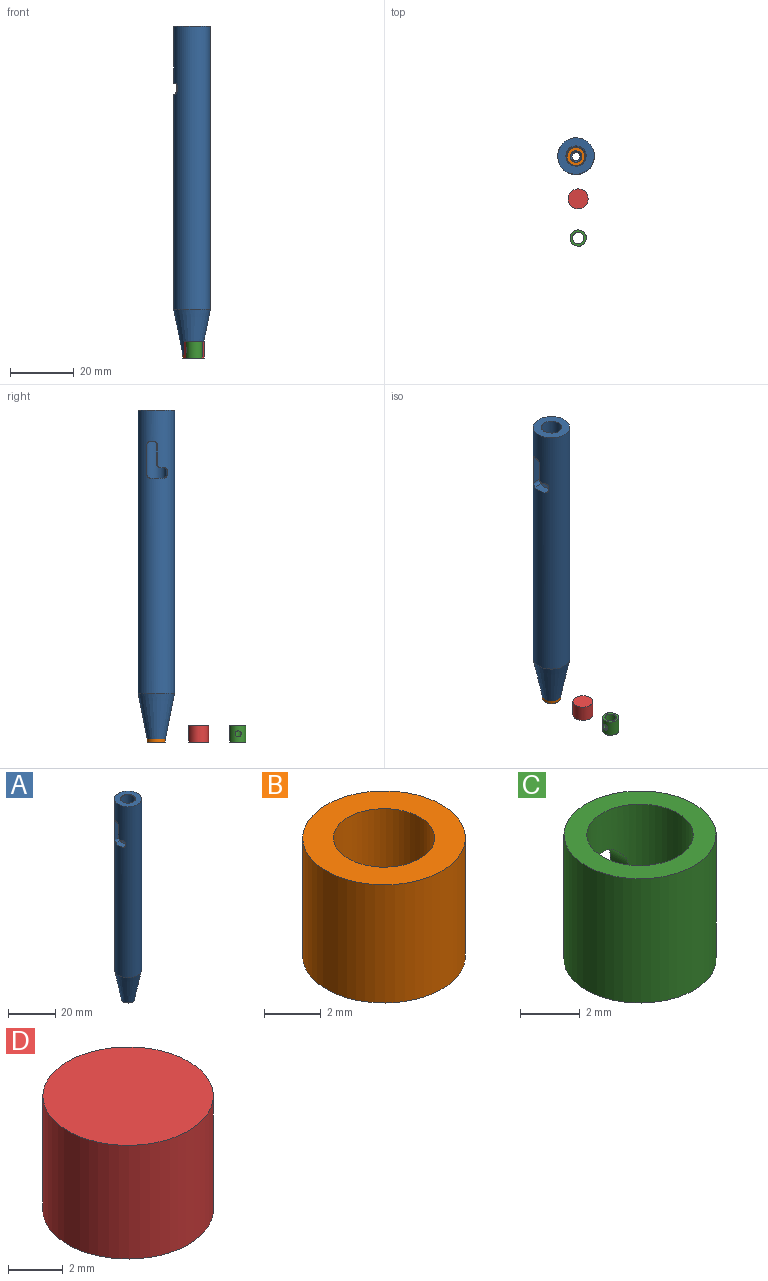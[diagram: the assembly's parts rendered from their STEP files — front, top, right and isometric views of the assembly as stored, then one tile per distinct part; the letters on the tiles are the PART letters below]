
ASSEMBLY  parts=4 mates=3
PART A: 22 faces, bbox 11.4x11.4x103.9 mm
  f0: cylinder r=1.78mm len=3.56mm, axis (0,0,-1), area 14.2mm2, adj f17,f20
  f1: cylinder r=3.17mm len=98.39mm, axis (0,0,-1), area 1893.3mm2, adj f3,f4,f5,f6,f7,f8,f10,f11
  f2: cylinder r=5.71mm len=88.61mm, axis (0,0,-1), area 3133.2mm2, adj f3,f4,f5,f6,f7,f8,f10,f11
  f3: plane 9.4x4.75mm, normal (0,-1,0), area 44.7mm2, adj f1,f2,f10,f15
  f4: plane 3.3x1.14mm, normal (0,0,-1), area 3.2mm2, adj f1,f2,f10,f11
  f5: plane 6.14x2.54mm, normal (0,1,0), area 15.6mm2, adj f1,f2,f11,f12
  f6: plane 3.21x0.99mm, normal (0,-0.08,-1), area 2.7mm2, adj f1,f2,f12,f13
  f7: plane 4.75x1.31mm, normal (0,1,0), area 6.2mm2, adj f1,f2,f13,f14
  f8: plane 4.32x3.39mm, normal (0,0,1), area 11.5mm2, adj f1,f2,f14,f15
  f9: plane 5.33x5.33mm, normal (0,0,-1), area 17.3mm2, adj f18,f19
  f10: cylinder r=1.02mm len=5.29mm, axis (-1,0,0), area 5.9mm2, adj f1,f2,f3,f4
  f11: cylinder r=1.02mm len=2.71mm, axis (-1,0,0), area 4.1mm2, adj f1,f2,f4,f5
  f12: cylinder r=1.02mm len=2.74mm, axis (-1,0,0), area 4.2mm2, adj f1,f2,f5,f6
  f13: cylinder r=1.02mm len=5.32mm, axis (-1,0,0), area 6.1mm2, adj f1,f2,f6,f7
  f14: cylinder r=1.02mm len=5.29mm, axis (1,0,0), area 5.9mm2, adj f1,f2,f7,f8
  f15: cylinder r=1.02mm len=5.29mm, axis (-1,0,0), area 5.9mm2, adj f1,f2,f3,f8
  f16: plane 11.43x11.43mm, normal (0,0,1), area 70.9mm2, adj f1,f2
  f17: plane 5.59x5.59mm, normal (0,0,1), area 14.6mm2, adj f0,f21
  f18: cone r=5.71mm half-angle=11.3deg, axis (0,0,1), area 409.3mm2, adj f2,f9
  f19: cylinder r=1.27mm len=3.3mm, axis (0,0,-1), area 26.3mm2, adj f9,f20
  f20: cone r=1.27mm half-angle=45deg, axis (0,0,1), area 6.9mm2, adj f0,f19
  f21: cone r=2.79mm half-angle=45deg, axis (0,0,1), area 10.1mm2, adj f1,f17
PART B: 4 faces, bbox 5.7x5.7x5.1 mm
  f0: cylinder r=1.78mm len=5.08mm, axis (0,0,-1), area 56.8mm2, adj f2,f3
  f1: cylinder r=2.86mm len=5.72mm, axis (0,0,-1), area 91.2mm2, adj f2,f3
  f2: plane 5.72x5.72mm, normal (0,0,1), area 15.7mm2, adj f0,f1
  f3: plane 5.72x5.72mm, normal (0,0,-1), area 15.7mm2, adj f0,f1
PART C: 5 faces, bbox 5.1x5.1x5.1 mm
  f0: cylinder r=1.78mm len=5.08mm, axis (0,0,-1), area 53.8mm2, adj f2,f3,f4
  f1: cylinder r=2.54mm len=5.08mm, axis (0,0,-1), area 78.2mm2, adj f2,f3,f4
  f2: plane 5.08x5.08mm, normal (0,0,1), area 10.3mm2, adj f0,f1
  f3: plane 5.08x5.08mm, normal (0,0,-1), area 10.3mm2, adj f0,f1
  f4: cylinder r=0.95mm len=1.91mm, axis (0,-1,0), area 4.8mm2, adj f0,f1
PART D: 3 faces, bbox 6.2x6.2x5.1 mm
  f0: cylinder r=3.11mm len=6.22mm, axis (0,0,-1), area 99.3mm2, adj f1,f2
  f1: plane 6.22x6.22mm, normal (0,0,1), area 30.4mm2, adj f0
  f2: plane 6.22x6.22mm, normal (0,0,-1), area 30.4mm2, adj f0
PLACE A rot(axis=(0,0,1),2.6deg) t=(-0.54,82.78,67.71)mm
PLACE B rot(axis=(0,0,1),2.6deg) t=(-0.54,82.78,16.91)mm
PLACE C rot(axis=(0,0,1),92.6deg) t=(0.13,57.28,16.91)mm
PLACE D rot(axis=(0,0,1),2.6deg) t=(0.14,69.56,16.91)mm
MATE planar B.f0 <-> A.f2  axis (0,0,-1) through (-0.54,82.78,16.91)mm
MATE planar A.f2 <-> C.f0  axis (0,0,-1) through (-0.54,82.78,16.91)mm
MATE planar D.f0 <-> A.f2  axis (0,0,-1) through (0.14,69.56,16.91)mm
